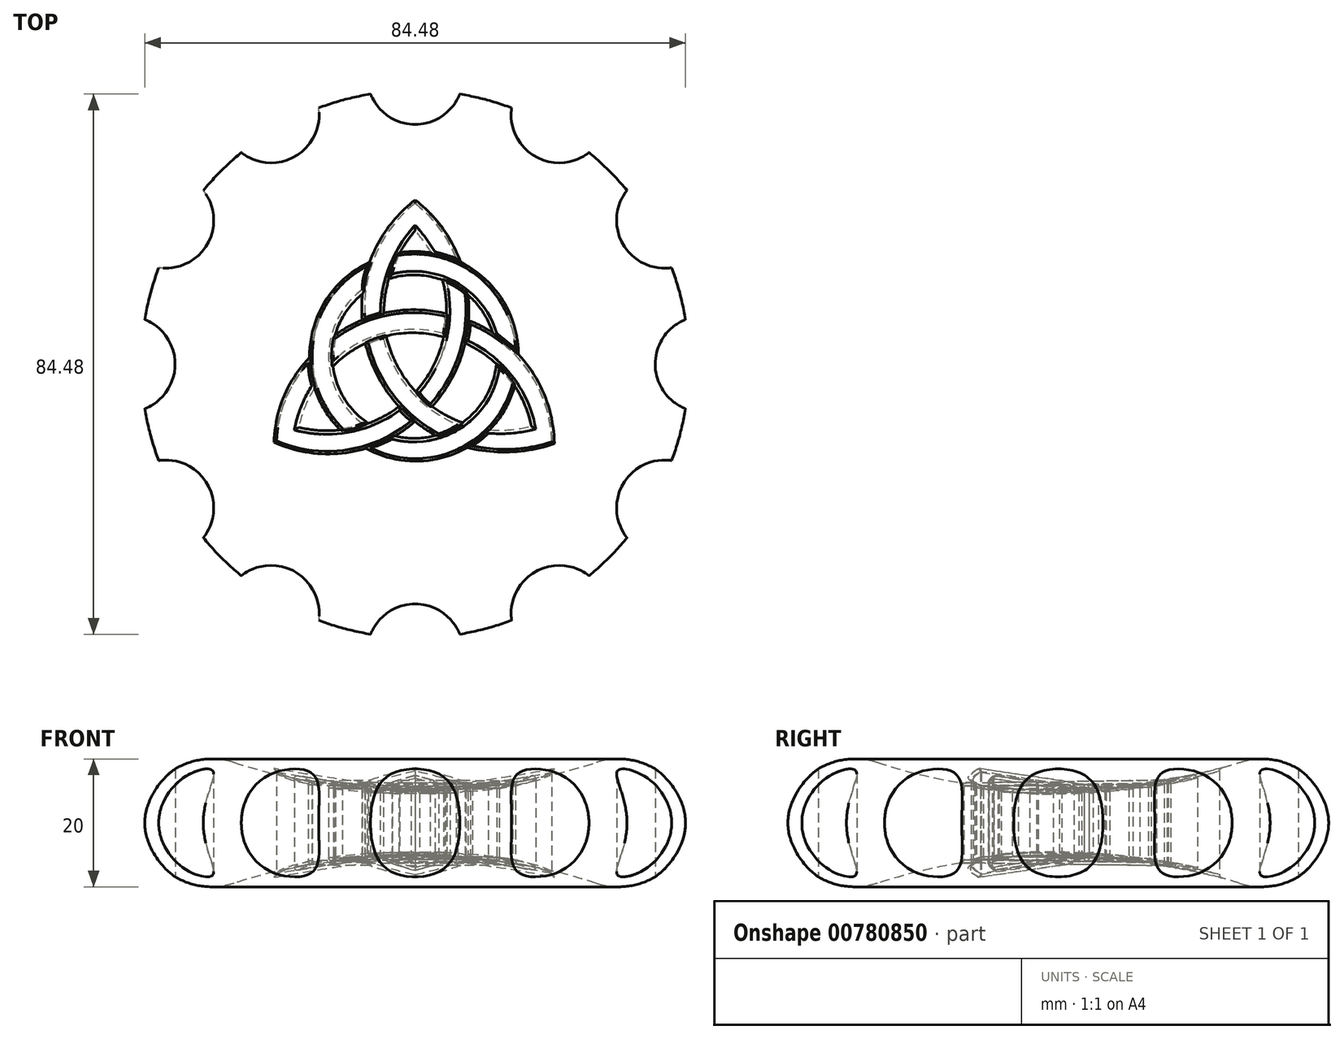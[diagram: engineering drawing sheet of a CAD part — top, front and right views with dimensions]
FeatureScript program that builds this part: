
annotation { "Feature Type Name" : "Feature", "Feature Type Description" : "" }
export const myFeature = defineFeature(function(context is Context, id is Id, definition is map)
    precondition{}
    {
        {
            var Q0;
            Q0=qCreatedBy(makeId("Front.planeOp"),FACE);
            var sketch = newSketch(context, id + "F0", { "sketchPlane" : qUnion([Q0])});
            skLineSegment(sketch, "E0", {"start": v(0, 0) * mm, "end": v(86, 0) * mm, "construction": true});
            skLineSegment(sketch, "E1", {"start": v(0, 0) * mm, "end": v(0, 5) * mm});
            skArc(sketch, "E2", {"start": v(0, 5) * mm, "mid": v(14.33, 6.12) * mm, "end": v(28.3, 9.45) * mm});
            skLineSegment(sketch, "E3", {"start": v(43, 0) * mm, "end": v(43, 47.92) * mm, "construction": true});
            skPoint(sketch, "E4.visualSharp", {"position": v(35, 11.9) * mm});
            skArc(sketch, "E4.filletArc", {"start": v(43, 0) * mm, "mid": v(37.9, 8.2) * mm, "end": v(28.3, 9.45) * mm});
            skLineSegment(sketch, "E5", {"start": v(31.8, 10) * mm, "end": v(31.78, 0) * mm, "construction": true});
            skLineSegment(sketch, "E6", {"start": v(0, 5) * mm, "end": v(-15.8, 5) * mm, "construction": true});
            skLineSegment(sketch, "E7.MirrorCS", {"start": v(0, 0) * mm, "end": v(0, -5) * mm});
            skArc(sketch, "E8.MirrorCS", {"start": v(0, -5) * mm, "mid": v(14.33, -6.12) * mm, "end": v(28.3, -9.45) * mm});
            skArc(sketch, "E9.MirrorCS", {"start": v(43, 0) * mm, "mid": v(37.9, -8.2) * mm, "end": v(28.3, -9.45) * mm});
            skSolve(sketch);
        }
        {
            var Q0;
            Q0 = qSketchRegion(id + "F0", true);
            var Q1;
            Q1=sQuery(id+"F0.wireOp",EDGE,"E7.MirrorCS");
            revolve(context, id + "F1", {"surfaceOperationType" : NewSurfaceOperationType.NEW, "entities" : qUnion([Q0]), "axis" : qUnion([Q1]), "revolveType" : RevolveType.FULL});
        }
        {
            var Q0;
            Q0=qCreatedBy(makeId("Top.planeOp"),FACE);
            var sketch = newSketch(context, id + "F2", { "sketchPlane" : qUnion([Q0])});
            skLineSegment(sketch, "E10", {"start": v(0, 0) * mm, "end": v(0, 70) * mm, "construction": true});
            skPoint(sketch, "E11", {"position": v(0, 45) * mm});
            skCircle(sketch, "E12", {"center": v(0, 45) * mm, "radius": 7.5 * mm});
            skCircle(sketch, "E13.1.0", {"center": v(-22.5, 38.97) * mm, "radius": 7.5 * mm});
            skCircle(sketch, "E13.2.0", {"center": v(-38.97, 22.5) * mm, "radius": 7.5 * mm});
            skCircle(sketch, "E13.3.0", {"center": v(-45, 0) * mm, "radius": 7.5 * mm});
            skCircle(sketch, "E13.4.0", {"center": v(-38.97, -22.5) * mm, "radius": 7.5 * mm});
            skCircle(sketch, "E13.5.0", {"center": v(-22.5, -38.97) * mm, "radius": 7.5 * mm});
            skCircle(sketch, "E13.6.0", {"center": v(0, -45) * mm, "radius": 7.5 * mm});
            skCircle(sketch, "E13.7.0", {"center": v(22.5, -38.97) * mm, "radius": 7.5 * mm});
            skCircle(sketch, "E13.8.0", {"center": v(38.97, -22.5) * mm, "radius": 7.5 * mm});
            skCircle(sketch, "E13.9.0", {"center": v(45, 0) * mm, "radius": 7.5 * mm});
            skCircle(sketch, "E13.10.0", {"center": v(38.97, 22.5) * mm, "radius": 7.5 * mm});
            skCircle(sketch, "E13.11.0", {"center": v(22.5, 38.97) * mm, "radius": 7.5 * mm});
            skPoint(sketch, "E13.center", {"position": v(0, 0) * mm});
            skSolve(sketch);
        }
        {
            var Q0;
            Q0 = qSketchRegion(id + "F2", true);
            extrude(context, id + "F3", {"entities" : qUnion([Q0]), "operationType" : NewBodyOperationType.REMOVE, "endBound" : BoundingType.SYMMETRIC, "depth" : 25 * mm, "offsetDistance" : 25 * mm});
        }
        {
            var Q0;
            Q0=qCreatedBy(makeId("Top.planeOp"),FACE);
            var sketch = newSketch(context, id + "F4", { "sketchPlane" : qUnion([Q0])});
            skLineSegment(sketch, "E14", {"start": v(101.2, 0) * mm, "end": v(142.11, 0) * mm, "construction": true});
            skPoint(sketch, "E14.startSnap0", {"position": v(101.2, -0.04) * mm});
            skPoint(sketch, "E15", {"position": v(0, 25.16) * mm});
            skArc(sketch, "E16", {"start": v(0, 25.16) * mm, "mid": v(-6.16, 17.2) * mm, "end": v(-7.83, 7.27) * mm});
            skArc(sketch, "E17", {"start": v(0, 21.73) * mm, "mid": v(-3.98, 15.38) * mm, "end": v(-5.44, 8.03) * mm});
            skArc(sketch, "E18", {"start": v(3.08, 17.56) * mm, "mid": v(1.65, 19.73) * mm, "end": v(0, 21.73) * mm});
            skArc(sketch, "E19", {"start": v(6.38, 16.57) * mm, "mid": v(3.76, 21.29) * mm, "end": v(0, 25.16) * mm});
            skArc(sketch, "E20", {"start": v(6.38, 16.57) * mm, "mid": v(4.74, 17.1) * mm, "end": v(3.08, 17.56) * mm});
            skArc(sketch, "E21", {"start": v(-5.44, 8.03) * mm, "mid": v(-6.65, 7.69) * mm, "end": v(-7.83, 7.27) * mm});
            skArc(sketch, "E22", {"start": v(-2.55, 17.01) * mm, "mid": v(-3.14, 15.58) * mm, "end": v(-3.58, 14.1) * mm});
            skArc(sketch, "E23", {"start": v(15.68, 2.44) * mm, "mid": v(9.78, 13.75) * mm, "end": v(-2.55, 17.01) * mm});
            skArc(sketch, "E24", {"start": v(12.75, 4.8) * mm, "mid": v(6.47, 12.76) * mm, "end": v(-3.58, 14.1) * mm});
            skArc(sketch, "E25", {"start": v(12.75, 4.8) * mm, "mid": v(14.2, 3.6) * mm, "end": v(15.68, 2.44) * mm});
            skArc(sketch, "E26", {"start": v(-7.51, 15.32) * mm, "mid": v(-8.08, 13.53) * mm, "end": v(-8.28, 11.67) * mm});
            skArc(sketch, "E27", {"start": v(-7.51, 15.32) * mm, "mid": v(-15.9, 3.62) * mm, "end": v(-11.34, -10.04) * mm});
            skArc(sketch, "E28", {"start": v(-11.34, -10.04) * mm, "mid": v(-9.79, -9.78) * mm, "end": v(-8.3, -9.24) * mm});
            skArc(sketch, "E29", {"start": v(-8.28, 11.67) * mm, "mid": v(-13.52, 1.22) * mm, "end": v(-8.3, -9.24) * mm});
            skArc(sketch, "E30", {"start": v(-12.46, 4.04) * mm, "mid": v(-12.7, 2.3) * mm, "end": v(-12.72, 0.55) * mm});
            skArc(sketch, "E31", {"start": v(4.67, 7.47) * mm, "mid": v(-4.28, 7.66) * mm, "end": v(-12.46, 4.04) * mm});
            skArc(sketch, "E32", {"start": v(4.42, 4.8) * mm, "mid": v(4.58, 6.13) * mm, "end": v(4.67, 7.47) * mm});
            skArc(sketch, "E33", {"start": v(4.42, 4.8) * mm, "mid": v(-4.7, 4.9) * mm, "end": v(-12.72, 0.55) * mm});
            skArc(sketch, "E34", {"start": v(0.67, -4.45) * mm, "mid": v(4.86, 3.65) * mm, "end": v(4.93, 12.76) * mm});
            skPoint(sketch, "E34.endSnap0", {"position": v(6.47, 12.76) * mm});
            skArc(sketch, "E35", {"start": v(0.67, -4.45) * mm, "mid": v(1.47, -5.4) * mm, "end": v(2.38, -6.24) * mm});
            skArc(sketch, "E36", {"start": v(2.38, -6.24) * mm, "mid": v(6.91, 1.8) * mm, "end": v(7.79, 11) * mm});
            skArc(sketch, "E37", {"start": v(7.79, 11) * mm, "mid": v(6.44, 12.01) * mm, "end": v(4.93, 12.76) * mm});
            skArc(sketch, "E38", {"start": v(15.2, -3.15) * mm, "mid": v(14.25, -1.9) * mm, "end": v(13.16, -0.76) * mm});
            skArc(sketch, "E39", {"start": v(-3.63, -11.72) * mm, "mid": v(7.2, -9.97) * mm, "end": v(13.16, -0.76) * mm});
            skArc(sketch, "E40", {"start": v(-7.02, -13.06) * mm, "mid": v(-5.26, -12.54) * mm, "end": v(-3.63, -11.72) * mm});
            skArc(sketch, "E41", {"start": v(-7.02, -13.06) * mm, "mid": v(6.46, -13.4) * mm, "end": v(15.2, -3.15) * mm});
            skArc(sketch, "E42", {"start": v(-2.43, -7.23) * mm, "mid": v(-1.6, -8.11) * mm, "end": v(-0.66, -8.9) * mm});
            skArc(sketch, "E43", {"start": v(-18.89, -10.3) * mm, "mid": v(-10.31, -10.63) * mm, "end": v(-2.43, -7.23) * mm});
            skArc(sketch, "E44", {"start": v(-16.16, -3.4) * mm, "mid": v(-17.85, -6.73) * mm, "end": v(-18.89, -10.3) * mm});
            skArc(sketch, "E45", {"start": v(-16.7, 0.19) * mm, "mid": v(-16.57, -1.63) * mm, "end": v(-16.16, -3.4) * mm});
            skArc(sketch, "E46", {"start": v(-16.7, 0.19) * mm, "mid": v(-20.24, -5.47) * mm, "end": v(-21.64, -12) * mm});
            skArc(sketch, "E47", {"start": v(-21.64, -12) * mm, "mid": v(-10.72, -13.4) * mm, "end": v(-0.66, -8.9) * mm});
            skArc(sketch, "E48", {"start": v(-4.96, 4.04) * mm, "mid": v(-6.16, 3.7) * mm, "end": v(-7.29, 3.2) * mm});
            skArc(sketch, "E49", {"start": v(-4.96, 4.04) * mm, "mid": v(-0.79, -4.1) * mm, "end": v(6.64, -9.44) * mm});
            skArc(sketch, "E50", {"start": v(3.7, -10.89) * mm, "mid": v(5.23, -10.28) * mm, "end": v(6.64, -9.44) * mm});
            skArc(sketch, "E51", {"start": v(-7.29, 3.2) * mm, "mid": v(-3.28, -5) * mm, "end": v(3.7, -10.89) * mm});
            skArc(sketch, "E52", {"start": v(8.92, -12.77) * mm, "mid": v(10.24, -11.88) * mm, "end": v(11.42, -10.8) * mm});
            skArc(sketch, "E53", {"start": v(8.92, -12.77) * mm, "mid": v(15.18, -13.3) * mm, "end": v(21.36, -12.16) * mm});
            skArc(sketch, "E54", {"start": v(21.36, -12.16) * mm, "mid": v(17.7, -1.09) * mm, "end": v(8.63, 6.24) * mm});
            skArc(sketch, "E55", {"start": v(8.26, 3.67) * mm, "mid": v(8.51, 4.94) * mm, "end": v(8.63, 6.24) * mm});
            skArc(sketch, "E56", {"start": v(18.85, -10.14) * mm, "mid": v(15.22, -1.96) * mm, "end": v(8.26, 3.67) * mm});
            skArc(sketch, "E57", {"start": v(11.42, -10.8) * mm, "mid": v(15.17, -10.8) * mm, "end": v(18.85, -10.14) * mm});
            skPoint(sketch, "E58", {"position": v(-0.1, 0.33) * mm});
            skSolve(sketch);
        }
        {
            var Q0;
            Q0 = qSketchRegion(id + "F4", true);
            extrude(context, id + "F5", {"entities" : qUnion([Q0]), "operationType" : NewBodyOperationType.REMOVE, "endBound" : BoundingType.SYMMETRIC, "depth" : 25 * mm, "offsetDistance" : 25 * mm});
        }
        {
            var Q0;
            Q0=makeQuery(id+"F1.opRevolve","SWEPT_FACE",FACE,{"disambiguationData":[OSD([sQuery(id+"F0.wireOp",EDGE,"E2")])]});
            var Q1;
            Q1=makeQuery(id+"F1.opRevolve","SWEPT_FACE",FACE,{"disambiguationData":[OSD([sQuery(id+"F0.wireOp",EDGE,"E8.MirrorCS")])]});
            fillet(context, id + "F6", {"entities" : qUnion([Q0, Q1]), "radius" : .5 * mm, "tangentPropagation" : true, "allowEdgeOverflow" : false});
        }
        {
            var Q0;
            {var subQ0=sQuery(id+"F0.wireOp",EDGE,"E4.filletArc");var subQ1=sQuery(id+"F0.wireOp",EDGE,"E9.MirrorCS");Q0=makeQuery(id+"F3.boolean.opBoolean","SPLIT",EDGE,{"disambiguationData":[TD([makeQuery(id+"F1.opRevolve","SWEPT_FACE",FACE,{"disambiguationData":[OSD([subQ0])]}),makeQuery(id+"F1.opRevolve","SWEPT_FACE",FACE,{"disambiguationData":[OSD([subQ1])]}),makeQuery(id+"F3.opExtrude","SWEPT_FACE",FACE,{"disambiguationData":[OSD([sQuery(id+"F2.wireOp",EDGE,"E13.1.0")])]}),makeQuery(id+"F3.opExtrude","SWEPT_FACE",FACE,{"disambiguationData":[OSD([sQuery(id+"F2.wireOp",EDGE,"E13.2.0")])]})])],"derivedFrom":makeQuery(id+"F1.opRevolve","SWEPT_EDGE",EDGE,{"disambiguationData":[OSD([subQ0,subQ1])]})});}
            var Q1;
            {var subQ0=sQuery(id+"F0.wireOp",EDGE,"E4.filletArc");var subQ1=sQuery(id+"F0.wireOp",EDGE,"E9.MirrorCS");Q1=makeQuery(id+"F3.boolean.opBoolean","SPLIT",EDGE,{"disambiguationData":[TD([makeQuery(id+"F1.opRevolve","SWEPT_FACE",FACE,{"disambiguationData":[OSD([subQ0])]}),makeQuery(id+"F1.opRevolve","SWEPT_FACE",FACE,{"disambiguationData":[OSD([subQ1])]}),makeQuery(id+"F3.opExtrude","SWEPT_FACE",FACE,{"disambiguationData":[OSD([sQuery(id+"F2.wireOp",EDGE,"E13.2.0")])]}),makeQuery(id+"F3.opExtrude","SWEPT_FACE",FACE,{"disambiguationData":[OSD([sQuery(id+"F2.wireOp",EDGE,"E13.3.0")])]})])],"derivedFrom":makeQuery(id+"F1.opRevolve","SWEPT_EDGE",EDGE,{"disambiguationData":[OSD([subQ0,subQ1])]})});}
            var Q2;
            {var subQ0=sQuery(id+"F0.wireOp",EDGE,"E4.filletArc");var subQ1=sQuery(id+"F0.wireOp",EDGE,"E9.MirrorCS");Q2=makeQuery(id+"F3.boolean.opBoolean","SPLIT",EDGE,{"disambiguationData":[TD([makeQuery(id+"F1.opRevolve","SWEPT_FACE",FACE,{"disambiguationData":[OSD([subQ0])]}),makeQuery(id+"F1.opRevolve","SWEPT_FACE",FACE,{"disambiguationData":[OSD([subQ1])]}),makeQuery(id+"F3.opExtrude","SWEPT_FACE",FACE,{"disambiguationData":[OSD([sQuery(id+"F2.wireOp",EDGE,"E13.3.0")])]}),makeQuery(id+"F3.opExtrude","SWEPT_FACE",FACE,{"disambiguationData":[OSD([sQuery(id+"F2.wireOp",EDGE,"E13.4.0")])]})])],"derivedFrom":makeQuery(id+"F1.opRevolve","SWEPT_EDGE",EDGE,{"disambiguationData":[OSD([subQ0,subQ1])]})});}
            var Q3;
            {var subQ0=sQuery(id+"F0.wireOp",EDGE,"E4.filletArc");var subQ1=sQuery(id+"F0.wireOp",EDGE,"E9.MirrorCS");Q3=makeQuery(id+"F3.boolean.opBoolean","SPLIT",EDGE,{"disambiguationData":[TD([makeQuery(id+"F1.opRevolve","SWEPT_FACE",FACE,{"disambiguationData":[OSD([subQ0])]}),makeQuery(id+"F1.opRevolve","SWEPT_FACE",FACE,{"disambiguationData":[OSD([subQ1])]}),makeQuery(id+"F3.opExtrude","SWEPT_FACE",FACE,{"disambiguationData":[OSD([sQuery(id+"F2.wireOp",EDGE,"E13.4.0")])]}),makeQuery(id+"F3.opExtrude","SWEPT_FACE",FACE,{"disambiguationData":[OSD([sQuery(id+"F2.wireOp",EDGE,"E13.5.0")])]})])],"derivedFrom":makeQuery(id+"F1.opRevolve","SWEPT_EDGE",EDGE,{"disambiguationData":[OSD([subQ0,subQ1])]})});}
            var Q4;
            {var subQ0=sQuery(id+"F0.wireOp",EDGE,"E4.filletArc");var subQ1=sQuery(id+"F0.wireOp",EDGE,"E9.MirrorCS");Q4=makeQuery(id+"F3.boolean.opBoolean","SPLIT",EDGE,{"disambiguationData":[TD([makeQuery(id+"F1.opRevolve","SWEPT_FACE",FACE,{"disambiguationData":[OSD([subQ0])]}),makeQuery(id+"F1.opRevolve","SWEPT_FACE",FACE,{"disambiguationData":[OSD([subQ1])]}),makeQuery(id+"F3.opExtrude","SWEPT_FACE",FACE,{"disambiguationData":[OSD([sQuery(id+"F2.wireOp",EDGE,"E13.5.0")])]}),makeQuery(id+"F3.opExtrude","SWEPT_FACE",FACE,{"disambiguationData":[OSD([sQuery(id+"F2.wireOp",EDGE,"E13.6.0")])]})])],"derivedFrom":makeQuery(id+"F1.opRevolve","SWEPT_EDGE",EDGE,{"disambiguationData":[OSD([subQ0,subQ1])]})});}
            var Q5;
            {var subQ0=sQuery(id+"F0.wireOp",EDGE,"E4.filletArc");var subQ1=sQuery(id+"F0.wireOp",EDGE,"E9.MirrorCS");Q5=makeQuery(id+"F3.boolean.opBoolean","SPLIT",EDGE,{"disambiguationData":[TD([makeQuery(id+"F1.opRevolve","SWEPT_FACE",FACE,{"disambiguationData":[OSD([subQ0])]}),makeQuery(id+"F1.opRevolve","SWEPT_FACE",FACE,{"disambiguationData":[OSD([subQ1])]}),makeQuery(id+"F3.opExtrude","SWEPT_FACE",FACE,{"disambiguationData":[OSD([sQuery(id+"F2.wireOp",EDGE,"E13.6.0")])]}),makeQuery(id+"F3.opExtrude","SWEPT_FACE",FACE,{"disambiguationData":[OSD([sQuery(id+"F2.wireOp",EDGE,"E13.7.0")])]})])],"derivedFrom":makeQuery(id+"F1.opRevolve","SWEPT_EDGE",EDGE,{"disambiguationData":[OSD([subQ0,subQ1])]})});}
            var Q6;
            {var subQ0=sQuery(id+"F0.wireOp",EDGE,"E4.filletArc");var subQ1=sQuery(id+"F0.wireOp",EDGE,"E9.MirrorCS");Q6=makeQuery(id+"F3.boolean.opBoolean","SPLIT",EDGE,{"disambiguationData":[TD([makeQuery(id+"F1.opRevolve","SWEPT_FACE",FACE,{"disambiguationData":[OSD([subQ0])]}),makeQuery(id+"F1.opRevolve","SWEPT_FACE",FACE,{"disambiguationData":[OSD([subQ1])]}),makeQuery(id+"F3.opExtrude","SWEPT_FACE",FACE,{"disambiguationData":[OSD([sQuery(id+"F2.wireOp",EDGE,"E13.7.0")])]}),makeQuery(id+"F3.opExtrude","SWEPT_FACE",FACE,{"disambiguationData":[OSD([sQuery(id+"F2.wireOp",EDGE,"E13.8.0")])]})])],"derivedFrom":makeQuery(id+"F1.opRevolve","SWEPT_EDGE",EDGE,{"disambiguationData":[OSD([subQ0,subQ1])]})});}
            var Q7;
            {var subQ0=sQuery(id+"F0.wireOp",EDGE,"E4.filletArc");var subQ1=sQuery(id+"F0.wireOp",EDGE,"E9.MirrorCS");Q7=makeQuery(id+"F3.boolean.opBoolean","SPLIT",EDGE,{"disambiguationData":[TD([makeQuery(id+"F1.opRevolve","SWEPT_FACE",FACE,{"disambiguationData":[OSD([subQ0])]}),makeQuery(id+"F1.opRevolve","SWEPT_FACE",FACE,{"disambiguationData":[OSD([subQ1])]}),makeQuery(id+"F3.opExtrude","SWEPT_FACE",FACE,{"disambiguationData":[OSD([sQuery(id+"F2.wireOp",EDGE,"E13.8.0")])]}),makeQuery(id+"F3.opExtrude","SWEPT_FACE",FACE,{"disambiguationData":[OSD([sQuery(id+"F2.wireOp",EDGE,"E13.9.0")])]})])],"derivedFrom":makeQuery(id+"F1.opRevolve","SWEPT_EDGE",EDGE,{"disambiguationData":[OSD([subQ0,subQ1])]})});}
            var Q8;
            {var subQ0=sQuery(id+"F0.wireOp",EDGE,"E4.filletArc");var subQ1=sQuery(id+"F0.wireOp",EDGE,"E9.MirrorCS");Q8=makeQuery(id+"F3.boolean.opBoolean","SPLIT",EDGE,{"disambiguationData":[TD([makeQuery(id+"F1.opRevolve","SWEPT_FACE",FACE,{"disambiguationData":[OSD([subQ0])]}),makeQuery(id+"F1.opRevolve","SWEPT_FACE",FACE,{"disambiguationData":[OSD([subQ1])]}),makeQuery(id+"F3.opExtrude","SWEPT_FACE",FACE,{"disambiguationData":[OSD([sQuery(id+"F2.wireOp",EDGE,"E13.9.0")])]}),makeQuery(id+"F3.opExtrude","SWEPT_FACE",FACE,{"disambiguationData":[OSD([sQuery(id+"F2.wireOp",EDGE,"E13.10.0")])]})])],"derivedFrom":makeQuery(id+"F1.opRevolve","SWEPT_EDGE",EDGE,{"disambiguationData":[OSD([subQ0,subQ1])]})});}
            var Q9;
            {var subQ0=sQuery(id+"F0.wireOp",EDGE,"E4.filletArc");var subQ1=sQuery(id+"F0.wireOp",EDGE,"E9.MirrorCS");Q9=makeQuery(id+"F3.boolean.opBoolean","SPLIT",EDGE,{"disambiguationData":[TD([makeQuery(id+"F1.opRevolve","SWEPT_FACE",FACE,{"disambiguationData":[OSD([subQ0])]}),makeQuery(id+"F1.opRevolve","SWEPT_FACE",FACE,{"disambiguationData":[OSD([subQ1])]}),makeQuery(id+"F3.opExtrude","SWEPT_FACE",FACE,{"disambiguationData":[OSD([sQuery(id+"F2.wireOp",EDGE,"E13.10.0")])]}),makeQuery(id+"F3.opExtrude","SWEPT_FACE",FACE,{"disambiguationData":[OSD([sQuery(id+"F2.wireOp",EDGE,"E13.11.0")])]})])],"derivedFrom":makeQuery(id+"F1.opRevolve","SWEPT_EDGE",EDGE,{"disambiguationData":[OSD([subQ0,subQ1])]})});}
            var Q10;
            {var subQ0=sQuery(id+"F0.wireOp",EDGE,"E4.filletArc");var subQ1=sQuery(id+"F0.wireOp",EDGE,"E9.MirrorCS");Q10=makeQuery(id+"F3.boolean.opBoolean","SPLIT",EDGE,{"disambiguationData":[TD([makeQuery(id+"F1.opRevolve","SWEPT_FACE",FACE,{"disambiguationData":[OSD([subQ0])]}),makeQuery(id+"F1.opRevolve","SWEPT_FACE",FACE,{"disambiguationData":[OSD([subQ1])]}),makeQuery(id+"F3.opExtrude","SWEPT_FACE",FACE,{"disambiguationData":[OSD([sQuery(id+"F2.wireOp",EDGE,"E12")])]}),makeQuery(id+"F3.opExtrude","SWEPT_FACE",FACE,{"disambiguationData":[OSD([sQuery(id+"F2.wireOp",EDGE,"E13.11.0")])]})])],"derivedFrom":makeQuery(id+"F1.opRevolve","SWEPT_EDGE",EDGE,{"disambiguationData":[OSD([subQ0,subQ1])]})});}
            var Q11;
            {var subQ0=sQuery(id+"F0.wireOp",EDGE,"E4.filletArc");var subQ1=sQuery(id+"F0.wireOp",EDGE,"E9.MirrorCS");Q11=makeQuery(id+"F3.boolean.opBoolean","SPLIT",EDGE,{"disambiguationData":[TD([makeQuery(id+"F1.opRevolve","SWEPT_FACE",FACE,{"disambiguationData":[OSD([subQ0])]}),makeQuery(id+"F1.opRevolve","SWEPT_FACE",FACE,{"disambiguationData":[OSD([subQ1])]}),makeQuery(id+"F3.opExtrude","SWEPT_FACE",FACE,{"disambiguationData":[OSD([sQuery(id+"F2.wireOp",EDGE,"E12")])]}),makeQuery(id+"F3.opExtrude","SWEPT_FACE",FACE,{"disambiguationData":[OSD([sQuery(id+"F2.wireOp",EDGE,"E13.1.0")])]})])],"derivedFrom":makeQuery(id+"F1.opRevolve","SWEPT_EDGE",EDGE,{"disambiguationData":[OSD([subQ0,subQ1])]})});}
            fillet(context, id + "F7", {"entities" : qUnion([Q0, Q1, Q2, Q3, Q4, Q5, Q6, Q7, Q8, Q9, Q10, Q11]), "radius" : 8 * mm, "tangentPropagation" : true, "allowEdgeOverflow" : false});
        }
    });
